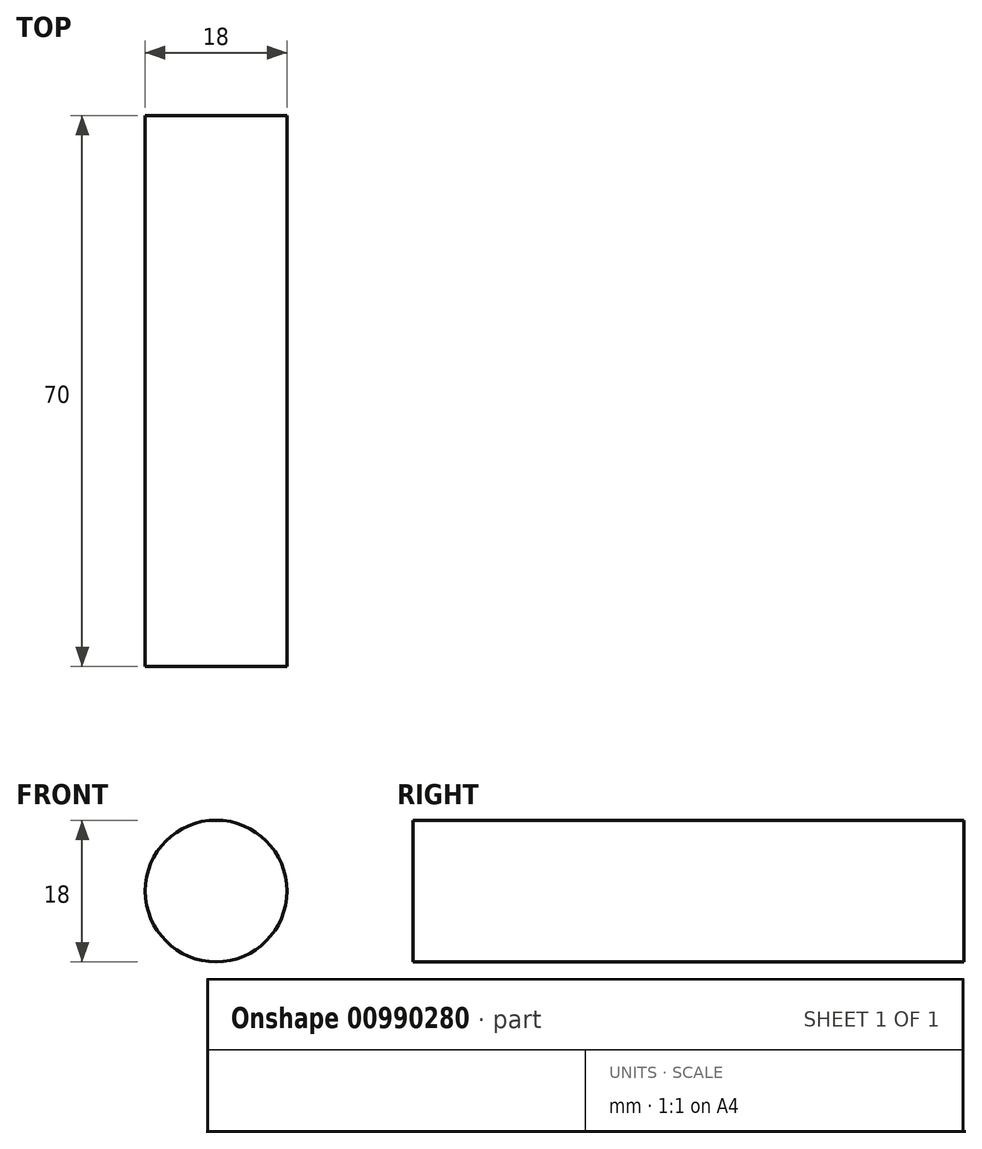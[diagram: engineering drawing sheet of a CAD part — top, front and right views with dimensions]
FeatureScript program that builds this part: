
annotation { "Feature Type Name" : "Feature", "Feature Type Description" : "" }
export const myFeature = defineFeature(function(context is Context, id is Id, definition is map)
    precondition{}
    {
        {
            var Q0;
            Q0=qCreatedBy(makeId("Front.planeOp"),FACE);
            var sketch = newSketch(context, id + "F0", { "sketchPlane" : qUnion([Q0])});
            skCircle(sketch, "E0", {"center": v(0, 0) * mm, "radius": 9 * mm});
            skSolve(sketch);
        }
        {
            var Q0;
            Q0=qSketchRegion(id+"F0",true);
            extrude(context, id + "F1", {"entities" : qUnion([Q0]), "depth" : 70 * mm, "offsetDistance" : 25 * mm});
        }
    });
